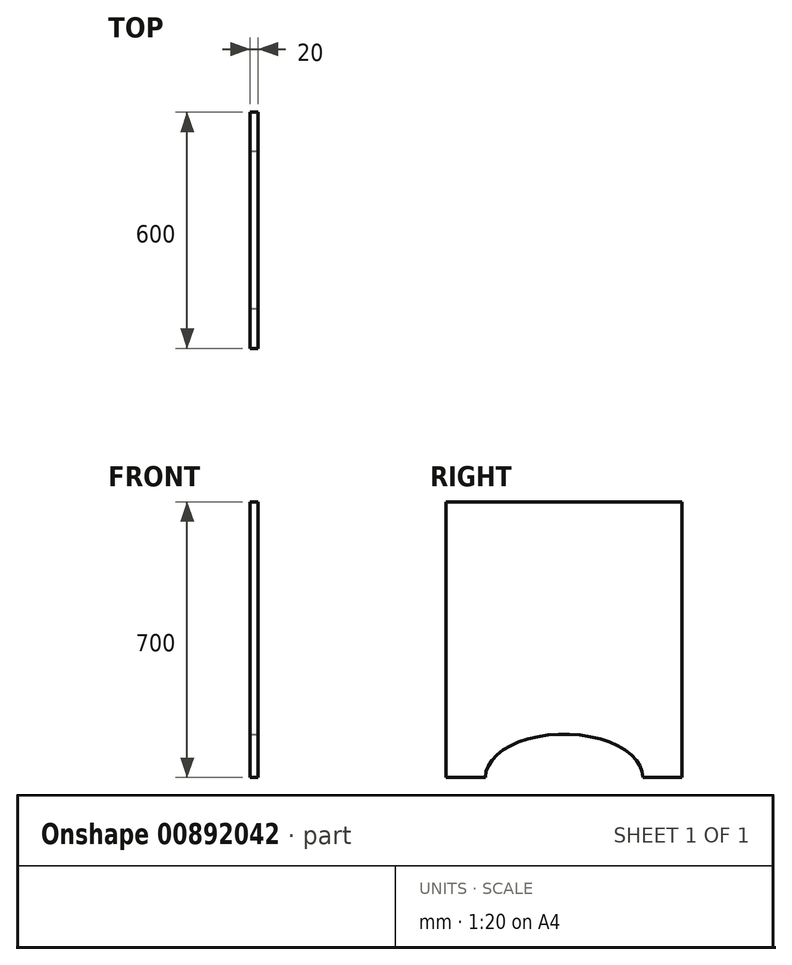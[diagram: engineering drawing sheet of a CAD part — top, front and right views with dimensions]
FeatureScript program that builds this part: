
annotation { "Feature Type Name" : "Feature", "Feature Type Description" : "" }
export const myFeature = defineFeature(function(context is Context, id is Id, definition is map)
    precondition{}
    {
        {
            var Q0;
            Q0=qCreatedBy(makeId("Right.planeOp"),FACE);
            var sketch = newSketch(context, id + "F0", { "sketchPlane" : qUnion([Q0])});
            skLineSegment(sketch, "E0.bottom", {"start": v(-355.35, -305.59) * mm, "end": v(244.65, -305.59) * mm});
            skLineSegment(sketch, "E0.top", {"start": v(-355.35, -1005.59) * mm, "end": v(244.65, -1005.59) * mm});
            skLineSegment(sketch, "E0.left", {"start": v(-355.35, -305.59) * mm, "end": v(-355.35, -1005.59) * mm});
            skLineSegment(sketch, "E0.right", {"start": v(244.65, -305.59) * mm, "end": v(244.65, -1005.59) * mm});
            skLineSegment(sketch, "E1", {"start": v(-355.35, -1005.59) * mm, "end": v(-255.35, -1005.59) * mm});
            skLineSegment(sketch, "E2", {"start": v(244.65, -1005.59) * mm, "end": v(144.65, -1005.59) * mm});
            skLineSegment(sketch, "E3", {"start": v(-255.35, -1005.59) * mm, "end": v(144.65, -1005.59) * mm});
            skEllipse(sketch, "E4", {"center": v(-55.35, -1005.59) * mm, "majorRadius": 200 * mm, "minorRadius": 109.67 * mm, "majorAxis": v(1, 0)});
            skSolve(sketch);
        }
        {
            var Q0;
            Q0=makeQuery(id+"F0.imprint","IMPRINT",FACE,{"disambiguationData":[TD([[makeQuery(id+"F0.imprint","IMPRINT",EDGE,{"derivedFrom":sQuery(id+"F0.wireOp",EDGE,"E0.bottom")}),-1.0]])]});
            extrude(context, id + "F1", {"entities" : qUnion([Q0]), "depth" : 20 * mm, "offsetDistance" : 25 * mm});
        }
    });
